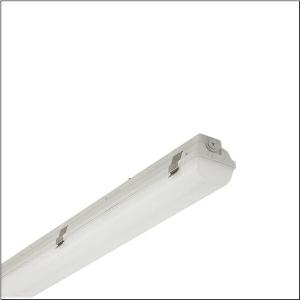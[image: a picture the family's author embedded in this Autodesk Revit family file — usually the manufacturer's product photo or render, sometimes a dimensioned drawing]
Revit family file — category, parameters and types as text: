
# Revit family: monsun_r__21_eco_51fj20ml45a_05e8
name_source: partatom
category: Lighting Fixtures
units: mm (PartAtom-declared; Revit-internal decimal feet)

## family parameters
Cut with Voids When Loaded = No
Host = Face
Light Source = No
Part Type = Normal
Room Calculation Point = No
Round Connector Dimension = Use Diameter
Shared = No

## types (1)
- --- (1 x LED, 4900 lm, 36 W, 4000K)
    Apparent Load = 36 VA
    CIE Flux Codes = 40 69 88 88 100
    Color Rendering = 80
    Color Temperature = 4000K
    Default Elevation = 1800 mm
    Description = Monsun® 21 Eco, damp-proof luminaire, primary optical cover: diffuser, of PC, UV-stabilised, frosted, light emission: direct distribution, primary light characteristic: symmetric, installation type: suspended mounting, surface-mounted, LED, rated luminous flux: 4.900lm, luminous efficacy: 132lm/W, light colour: 840, colour temperature: 4000K, control gear: ECG Multilumen, with terminal, 3-pole, max. 2.5mm², mains connection: 220..240V, AC, 50/60Hz, rated input power: 36W, housing, of glass-fibre reinforced polyester, light grey (RAL 7035), length: 1.277mm, width: 90mm, height: 95mm, clip for enclosure, of spring steel V2A, protection rating (complete): IP66, insulation class (complete): insulation class I (protective earthing), certification: CE, UKCA, protection symbol: D, impact resistance: IK08, permissible operating ambient temperature: -20..+35°C, corresponds to IFS (International Featured Standards) requirements for safety and quality in the food industry, contact your sales advisor before using the luminaires in applications with unclear chemical exposure, large temperature fluctuations or condensation-forming humidity, packaging unit: 1 piece
    Height = 103 mm
    Lamp = 1 x LED
    Lamp Light Flux = 4900 lm
    Lamp Power = 36 W
    Lamp count = 1
    Length = 1277 mm
    Luminous efficacy = 136 lm/W
    Manufacturer = Siteco
    ModVariant = No
    Model = 51FJ20ML45A
    Mounting Place = Ceiling
    Mounting Type = Surface mounted
    Number of Poles = 1
    OnlyDefault = Yes
    Power Factor = 1
    Product Name = Monsun® 21 Eco
    Product group = damp-proof luminaire
    ProductGroupID = 301
    Protection Class = Protection class I
    Protection Degree = IP 66
    RLX_Detail_Level = 1
    RLX_Emergency_Light_Flux = 0 lm
    RLX_Emergency_Type = 0
    RLX_Emergency_Type_DB = No
    RlxData = <blob elided: 34105 chars, md5=9c459d13>
    Socket = socket
    Standby Power = 0 W
    System Light Flux = 4900 lm
    System Power = 36 W
    Type Comments = factory setting: luminous flux: 100 % | (ON | ON) | 350 mA
    Type Image = l_1007218.jpg
    URL = http://relux.com
    VarID = @adj_095753
    Voltage = 0 V
    Weight = 0.00 kg
    Width = 90 mm

## geometry (parser evidence)
native form markers: Blend x4, Sweep x13
no freeform markers — native parametric forms only
